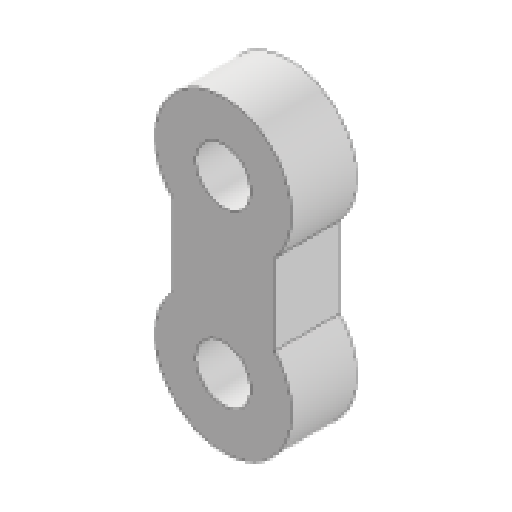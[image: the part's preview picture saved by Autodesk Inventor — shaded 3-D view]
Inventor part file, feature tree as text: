
AUTODESK INVENTOR PART (.ipt)
format: ipt  version: 2025 (Build 290162010, 162A)  size: 105,984 bytes
history: native  units: in
note: dims shown in document units (in); Inventor stores cm internally (conversion verified against a paired STEP export)
features: extrude x1, sketch x1
ambient origin geometry x8: Origin, YZ Plane, XZ Plane, XY Plane, X Axis, Y Axis, Z Axis, Center Point
bodies: Solid1 (feature_tree)
feature tree (2):
  extrude  "Extrusion1"  Depth=0.3in
  sketch  "Sketch1"  dims[d0=0.16in d1=0.4in d3=0.16in d4=0.4in d5=0.5in d6=0.19in d7=0.0in d31=0.2in d34=0.3in d35=0.15in]
